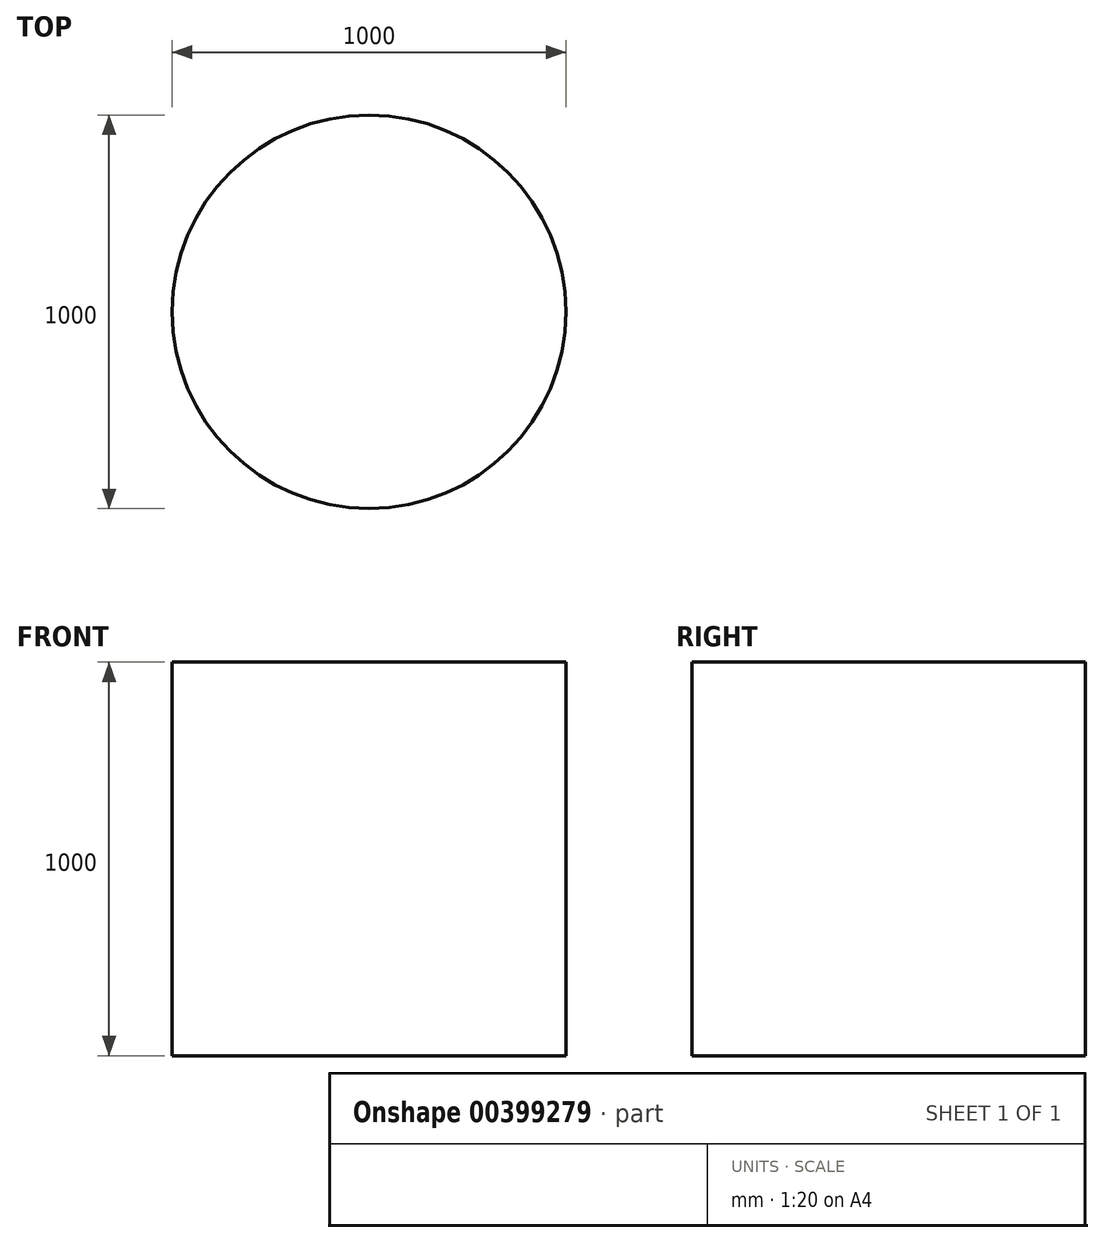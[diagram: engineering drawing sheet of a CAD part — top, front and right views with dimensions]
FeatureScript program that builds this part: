
annotation { "Feature Type Name" : "Feature", "Feature Type Description" : "" }
export const myFeature = defineFeature(function(context is Context, id is Id, definition is map)
    precondition{}
    {
        {
            var Q0;
            Q0=qCreatedBy(makeId("Top.planeOp"),FACE);
            var sketch = newSketch(context, id + "F0", { "sketchPlane" : qUnion([Q0])});
            skCircle(sketch, "E0", {"center": v(0, 0) * mm, "radius": 500 * mm});
            skSolve(sketch);
        }
        {
            var Q0;
            Q0=makeQuery(id+"F0.imprint","IMPRINT",FACE,{"disambiguationData":[TD([[makeQuery(id+"F0.imprint","IMPRINT",EDGE,{"derivedFrom":sQuery(id+"F0.wireOp",EDGE,"E0")}),1.0]])]});
            extrude(context, id + "F1", {"entities" : qUnion([Q0]), "depth" : 1000 * mm});
        }
    });
